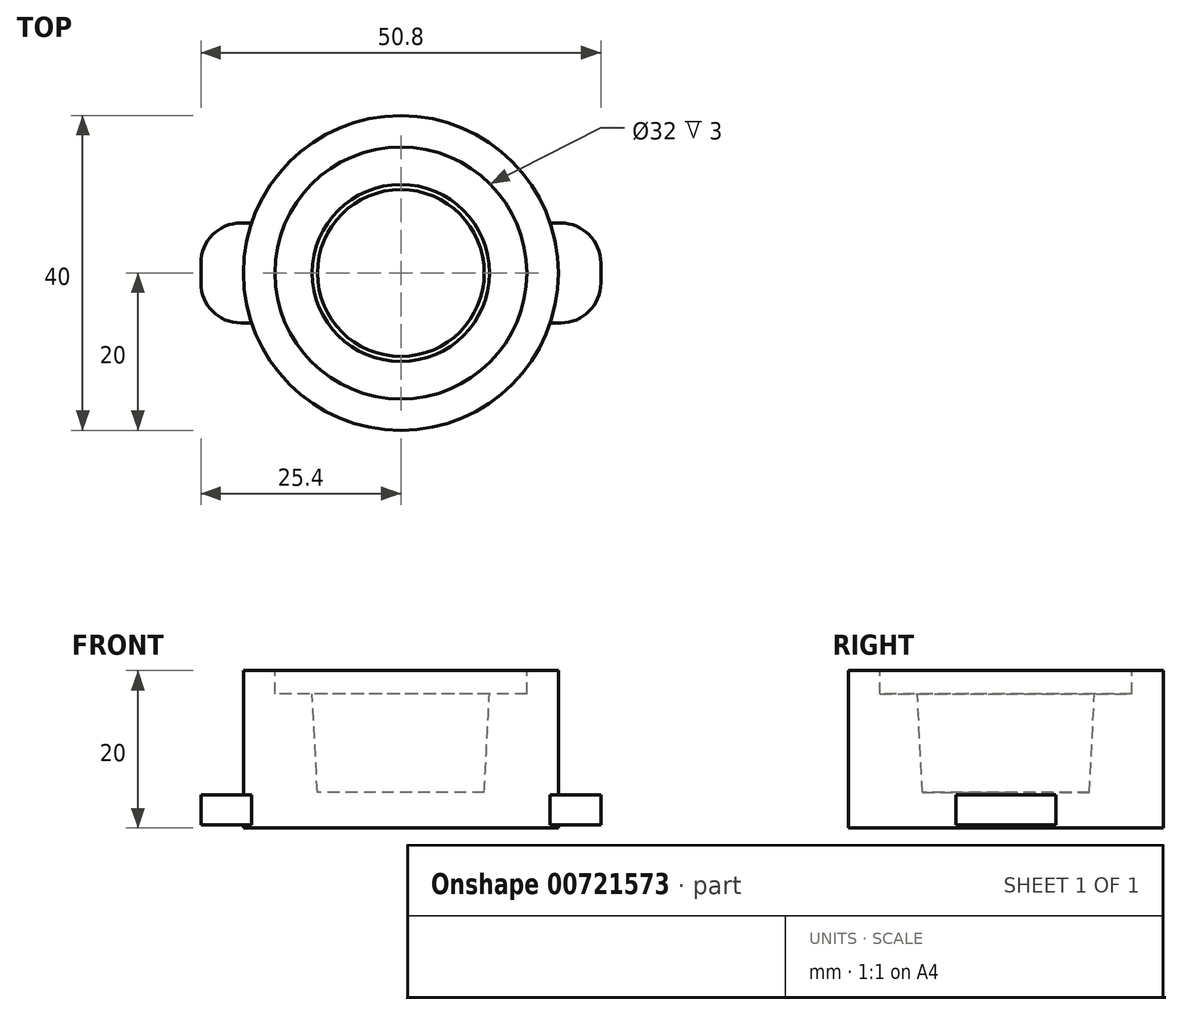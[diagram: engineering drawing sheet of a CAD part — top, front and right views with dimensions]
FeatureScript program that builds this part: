
annotation { "Feature Type Name" : "Feature", "Feature Type Description" : "" }
export const myFeature = defineFeature(function(context is Context, id is Id, definition is map)
    precondition{}
    {
        {
            var Q0;
            Q0=qCreatedBy(makeId("Top.planeOp"),FACE);
            var sketch = newSketch(context, id + "F0", { "sketchPlane" : qUnion([Q0])});
            skCircle(sketch, "E0", {"center": v(0, 0) * mm, "radius": 20 * mm});
            skSolve(sketch);
        }
        {
            var Q0;
            Q0=makeQuery(id+"F0.imprint","IMPRINT",FACE,{"disambiguationData":[TD([[makeQuery(id+"F0.imprint","IMPRINT",EDGE,{"derivedFrom":sQuery(id+"F0.wireOp",EDGE,"E0")}),1.0]])]});
            extrude(context, id + "F1", {"entities" : qUnion([Q0]), "oppositeDirection" : true, "depth" : 20 * mm, "offsetDistance" : 25.4 * mm});
        }
        {
            var Q0;
            Q0=makeQuery(id+"F1.opExtrude","CAP_FACE",FACE,{"disambiguationData":[OSD([sQuery(id+"F0.wireOp",EDGE,"E0")])],"isStart":true});
            var sketch = newSketch(context, id + "F2", { "sketchPlane" : qUnion([Q0])});
            skCircle(sketch, "E1", {"center": v(0, 0) * mm, "radius": 16 * mm});
            skSolve(sketch);
        }
        {
            var Q0;
            Q0=makeQuery(id+"F2.imprint","IMPRINT",FACE,{"disambiguationData":[TD([[makeQuery(id+"F2.imprint","IMPRINT",EDGE,{"derivedFrom":sQuery(id+"F2.wireOp",EDGE,"E1")}),1.0]])]});
            extrude(context, id + "F3", {"entities" : qUnion([Q0]), "operationType" : NewBodyOperationType.REMOVE, "oppositeDirection" : true, "depth" : 3 * mm, "offsetDistance" : 25.4 * mm});
        }
        {
            var Q0;
            Q0=makeQuery(id+"F3.boolean.opBoolean","COPY",FACE,{"derivedFrom":makeQuery(id+"F3.opExtrude","CAP_FACE",FACE,{"disambiguationData":[OSD([sQuery(id+"F2.wireOp",EDGE,"E1")])],"isStart":false})});
            var sketch = newSketch(context, id + "F4", { "sketchPlane" : qUnion([Q0])});
            skCircle(sketch, "E2", {"center": v(0, 0) * mm, "radius": 11.25 * mm});
            skSolve(sketch);
        }
        {
            var Q0;
            Q0=makeQuery(id+"F4.imprint","IMPRINT",FACE,{"disambiguationData":[TD([[makeQuery(id+"F4.imprint","IMPRINT",EDGE,{"derivedFrom":sQuery(id+"F4.wireOp",EDGE,"E2")}),1.0]])]});
            extrude(context, id + "F5", {"entities" : qUnion([Q0]), "operationType" : NewBodyOperationType.REMOVE, "oppositeDirection" : true, "depth" : 12.5 * mm, "offsetDistance" : 25.4 * mm, "hasDraft" : true, "draftAngle" : 3 * degree, "draftPullDirection" : true});
        }
        {
            var Q0;
            Q0=qCreatedBy(makeId("Right.planeOp"),FACE);
            var sketch = newSketch(context, id + "F6", { "sketchPlane" : qUnion([Q0])});
            skLineSegment(sketch, "E3.bottom", {"start": v(-6.35, -15.79) * mm, "end": v(6.35, -15.79) * mm});
            skLineSegment(sketch, "E3.top", {"start": v(-6.35, -19.6) * mm, "end": v(6.35, -19.6) * mm});
            skLineSegment(sketch, "E3.left", {"start": v(-6.35, -15.79) * mm, "end": v(-6.35, -19.6) * mm});
            skLineSegment(sketch, "E3.right", {"start": v(6.35, -15.79) * mm, "end": v(6.35, -19.6) * mm});
            skSolve(sketch);
        }
        {
            var Q0;
            Q0 = qSketchRegion(id + "F6", true);
            extrude(context, id + "F7", {"entities" : qUnion([Q0]), "operationType" : NewBodyOperationType.ADD, "depth" : 25.4 * mm, "offsetDistance" : 25.4 * mm});
        }
        {
            var Q0;
            Q0 = qSketchRegion(id + "F6", true);
            extrude(context, id + "F8", {"entities" : qUnion([Q0]), "operationType" : NewBodyOperationType.ADD, "oppositeDirection" : true, "depth" : 25.4 * mm, "offsetDistance" : 25.4 * mm});
        }
        {
            var Q0;
            Q0=makeQuery(id+"F8.opExtrude","CAP_EDGE",EDGE,{"disambiguationData":[OSD([sQuery(id+"F6.wireOp",EDGE,"E3.right")])],"isStart":false});
            var Q1;
            Q1=makeQuery(id+"F8.opExtrude","CAP_EDGE",EDGE,{"disambiguationData":[OSD([sQuery(id+"F6.wireOp",EDGE,"E3.left")])],"isStart":false});
            var Q2;
            Q2=makeQuery(id+"F7.opExtrude","CAP_EDGE",EDGE,{"disambiguationData":[OSD([sQuery(id+"F6.wireOp",EDGE,"E3.left")])],"isStart":false});
            var Q3;
            Q3=makeQuery(id+"F7.opExtrude","CAP_EDGE",EDGE,{"disambiguationData":[OSD([sQuery(id+"F6.wireOp",EDGE,"E3.right")])],"isStart":false});
            fillet(context, id + "F9", {"entities" : qUnion([Q0, Q1, Q2, Q3]), "radius" : 5.08 * mm, "tangentPropagation" : true, "allowEdgeOverflow" : false});
        }
    });
